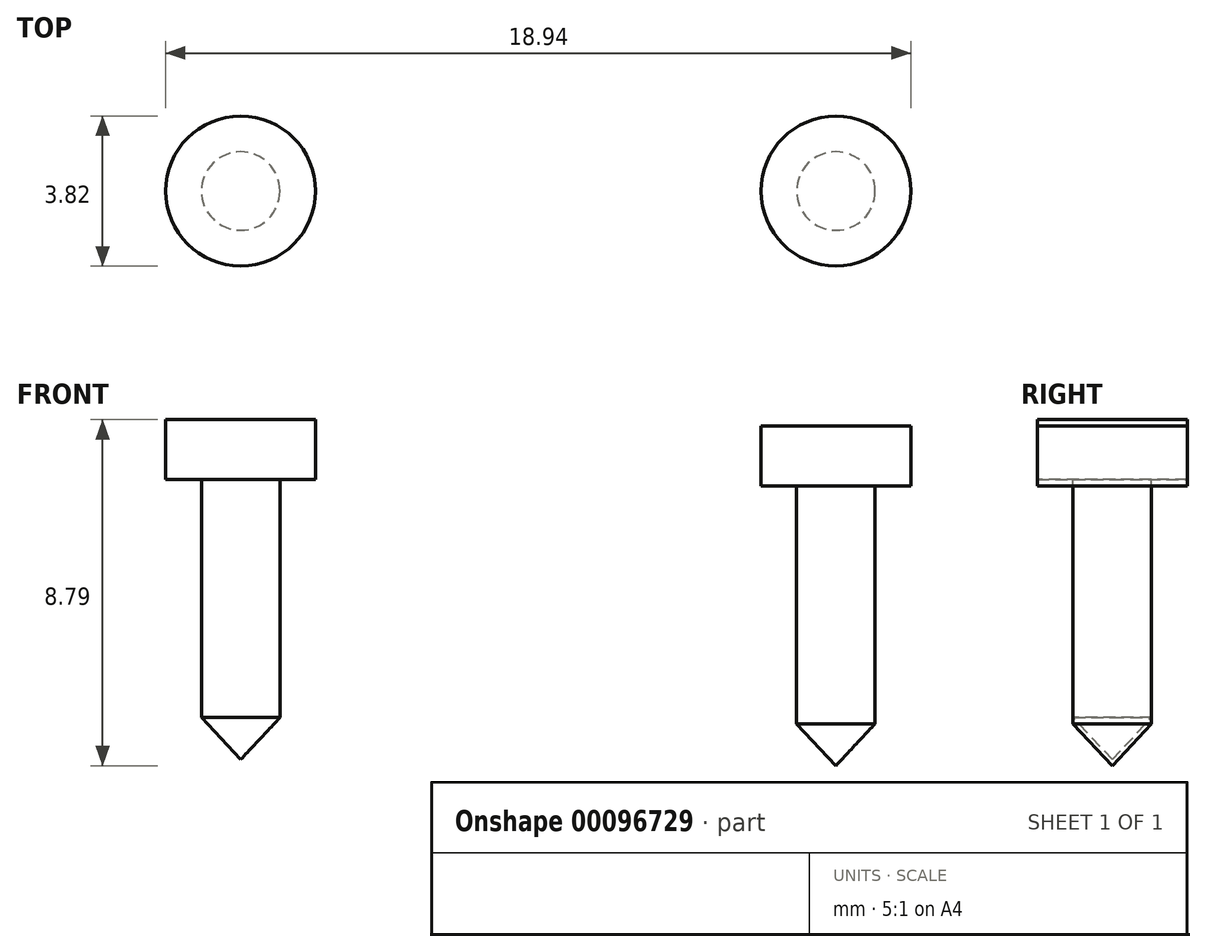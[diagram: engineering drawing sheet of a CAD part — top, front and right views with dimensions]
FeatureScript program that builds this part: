
annotation { "Feature Type Name" : "Feature", "Feature Type Description" : "" }
export const myFeature = defineFeature(function(context is Context, id is Id, definition is map)
    precondition{}
    {
        {
            var Q0;
            Q0=qCreatedBy(makeId("Front.planeOp"),FACE);
            var sketch = newSketch(context, id + "F0", { "sketchPlane" : qUnion([Q0])});
            skLineSegment(sketch, "E0", {"start": v(0, 0) * mm, "end": v(1, 1.07) * mm});
            skLineSegment(sketch, "E1", {"start": v(1, 1.07) * mm, "end": v(1, 7.11) * mm});
            skLineSegment(sketch, "E2", {"start": v(1, 7.11) * mm, "end": v(1.9, 7.11) * mm});
            skLineSegment(sketch, "E3", {"start": v(1.9, 7.11) * mm, "end": v(1.9, 8.64) * mm});
            skLineSegment(sketch, "E4", {"start": v(1.9, 8.64) * mm, "end": v(0, 8.64) * mm});
            skLineSegment(sketch, "E5", {"start": v(0, 8.64) * mm, "end": v(0, 0) * mm});
            skSolve(sketch);
        }
        {
            var Q0;
            Q0 = qSketchRegion(id + "F0", true);
            var Q1;
            Q1=sQuery(id+"F0.wireOp",EDGE,"E5");
            revolve(context, id + "F1", {"entities" : qUnion([Q0]), "axis" : qUnion([Q1]), "revolveType" : RevolveType.FULL});
        }
        {
            var Q0;
            Q0=qCreatedBy(makeId("Front.planeOp"),FACE);
            var sketch = newSketch(context, id + "F2", { "sketchPlane" : qUnion([Q0])});
            skLineSegment(sketch, "E6", {"start": v(-15.12, 0.15) * mm, "end": v(-14.12, 1.22) * mm});
            skLineSegment(sketch, "E7", {"start": v(-14.12, 1.22) * mm, "end": v(-14.12, 7.27) * mm});
            skLineSegment(sketch, "E8", {"start": v(-14.12, 7.27) * mm, "end": v(-13.22, 7.27) * mm});
            skLineSegment(sketch, "E9", {"start": v(-13.22, 7.27) * mm, "end": v(-13.22, 8.8) * mm});
            skLineSegment(sketch, "E10", {"start": v(-13.22, 8.8) * mm, "end": v(-15.12, 8.8) * mm});
            skLineSegment(sketch, "E11", {"start": v(-15.12, 8.8) * mm, "end": v(-15.12, 0.15) * mm});
            skSolve(sketch);
        }
        {
            var Q0;
            Q0=makeQuery(id+"F2.imprint","IMPRINT",FACE,{"disambiguationData":[TD([[makeQuery(id+"F2.imprint","IMPRINT",EDGE,{"derivedFrom":sQuery(id+"F2.wireOp",EDGE,"E6")}),1.0]])]});
            var Q1;
            Q1=sQuery(id+"F2.wireOp",EDGE,"E11");
            revolve(context, id + "F3", {"entities" : qUnion([Q0]), "axis" : qUnion([Q1]), "revolveType" : RevolveType.FULL});
        }
    });
